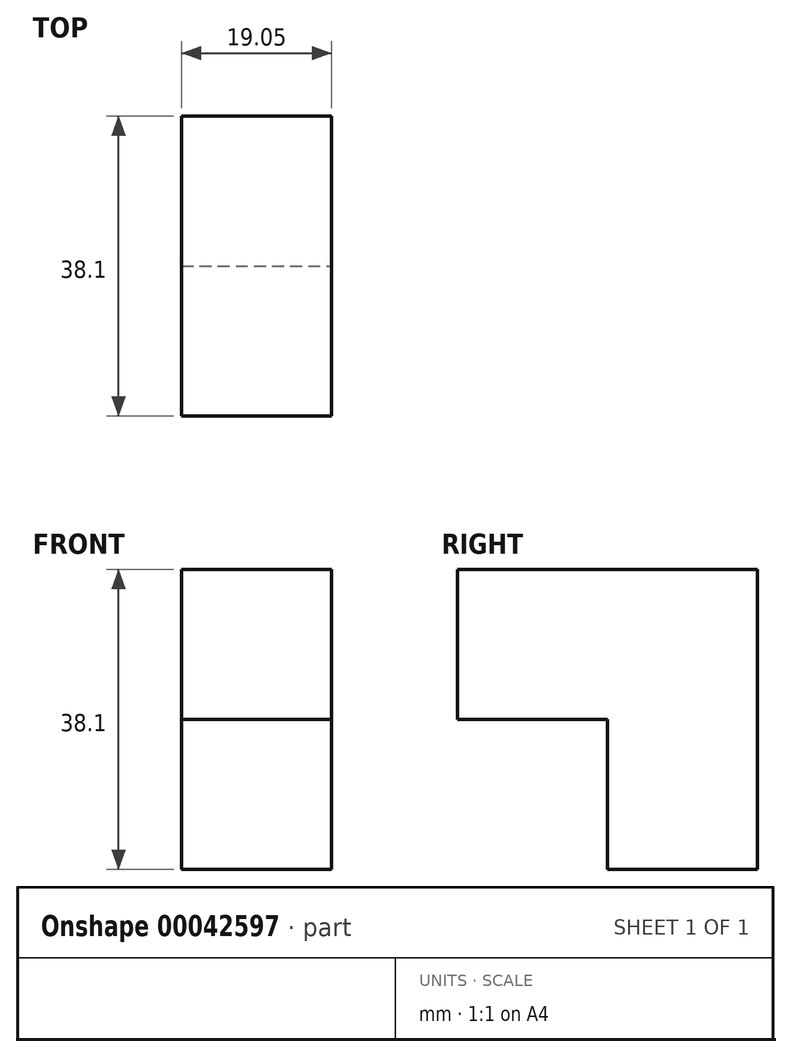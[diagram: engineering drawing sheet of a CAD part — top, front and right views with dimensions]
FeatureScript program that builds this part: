
annotation { "Feature Type Name" : "Feature", "Feature Type Description" : "" }
export const myFeature = defineFeature(function(context is Context, id is Id, definition is map)
    precondition{}
    {
        {
            var Q0;
            Q0=qCreatedBy(makeId("Top.planeOp"),FACE);
            var sketch = newSketch(context, id + "F0", { "sketchPlane" : qUnion([Q0])});
            skLineSegment(sketch, "E0.bottom", {"start": v(-45.24, -31.05) * mm, "end": v(-26.19, -31.05) * mm});
            skLineSegment(sketch, "E0.top", {"start": v(-45.24, -50.1) * mm, "end": v(-26.19, -50.1) * mm});
            skLineSegment(sketch, "E0.left", {"start": v(-45.24, -31.05) * mm, "end": v(-45.24, -50.1) * mm});
            skLineSegment(sketch, "E0.right", {"start": v(-26.19, -31.05) * mm, "end": v(-26.19, -50.1) * mm});
            skSolve(sketch);
        }
        {
            var Q0;
            Q0 = qSketchRegion(id + "F0", true);
            extrude(context, id + "F1", {"entities" : qUnion([Q0]), "depth" : 38.1 * mm});
        }
        {
            var Q0;
            Q0=makeQuery(id+"F1.opExtrude","SWEPT_FACE",FACE,{"disambiguationData":[OSD([sQuery(id+"F0.wireOp",EDGE,"E0.top")])]});
            var sketch = newSketch(context, id + "F2", { "sketchPlane" : qUnion([Q0])});
            skLineSegment(sketch, "E1.bottom", {"start": v(-45.24, 38.1) * mm, "end": v(-26.19, 38.1) * mm});
            skLineSegment(sketch, "E1.top", {"start": v(-45.24, 19.05) * mm, "end": v(-26.19, 19.05) * mm});
            skLineSegment(sketch, "E1.left", {"start": v(-45.24, 38.1) * mm, "end": v(-45.24, 19.05) * mm});
            skLineSegment(sketch, "E1.right", {"start": v(-26.19, 38.1) * mm, "end": v(-26.19, 19.05) * mm});
            skSolve(sketch);
        }
        {
            var Q0;
            Q0 = qSketchRegion(id + "F2", true);
            extrude(context, id + "F3", {"entities" : qUnion([Q0]), "operationType" : NewBodyOperationType.ADD, "depth" : 19.05 * mm});
        }
    });
